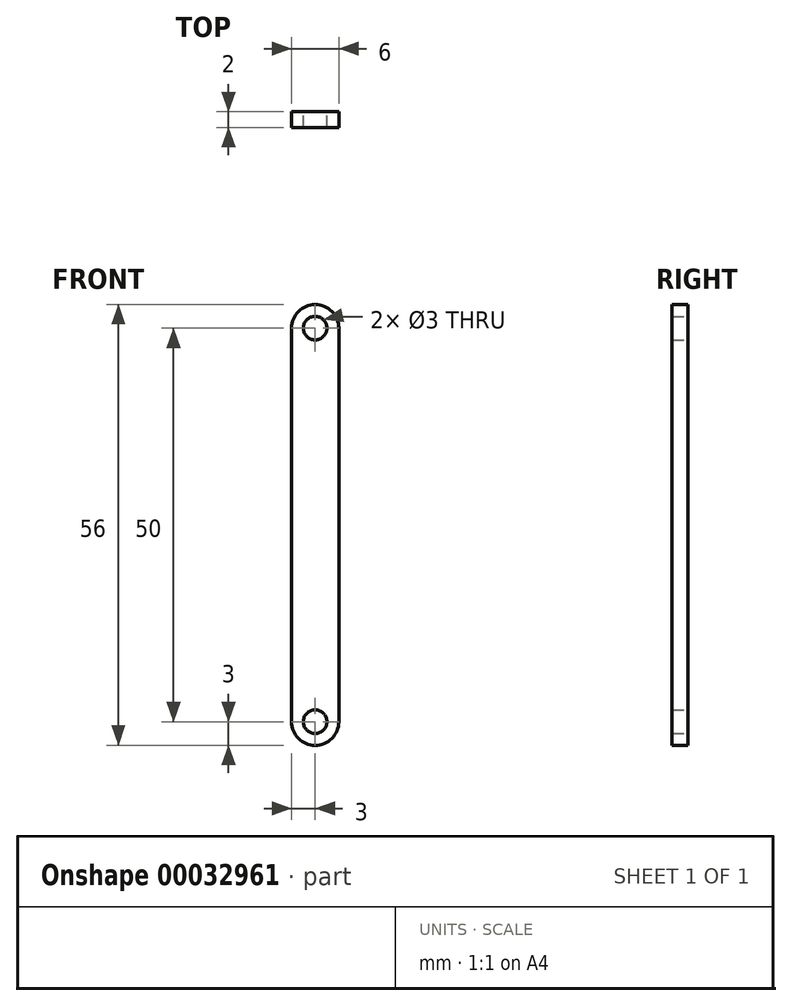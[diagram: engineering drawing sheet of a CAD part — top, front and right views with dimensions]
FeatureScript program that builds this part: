
annotation { "Feature Type Name" : "Feature", "Feature Type Description" : "" }
export const myFeature = defineFeature(function(context is Context, id is Id, definition is map)
    precondition{}
    {
        {
            var Q0;
            Q0=qCreatedBy(makeId("Front.planeOp"),FACE);
            var sketch = newSketch(context, id + "F0", { "sketchPlane" : qUnion([Q0])});
            skLineSegment(sketch, "E0.rect.left", {"start": v(3, -25) * mm, "end": v(3, 25) * mm});
            skLineSegment(sketch, "E0.rect.right", {"start": v(-3, -25) * mm, "end": v(-3, 25) * mm});
            skPoint(sketch, "E0.rect.middle", {"position": v(0, 0) * mm});
            skArc(sketch, "E1", {"start": v(3, 25) * mm, "mid": v(0, 28) * mm, "end": v(-3, 25) * mm});
            skArc(sketch, "E2.MirrorCS", {"start": v(3, -25) * mm, "mid": v(0, -28) * mm, "end": v(-3, -25) * mm});
            skCircle(sketch, "E3", {"center": v(0, 25) * mm, "radius": 1.5 * mm});
            skCircle(sketch, "E4.MirrorC", {"center": v(0, -25) * mm, "radius": 1.5 * mm});
            skSolve(sketch);
        }
        {
            var Q0;
            Q0=qSketchRegion(id+"F0",true);
            extrude(context, id + "F1", {"entities" : qUnion([Q0]), "depth" : 2 * mm});
        }
    });
